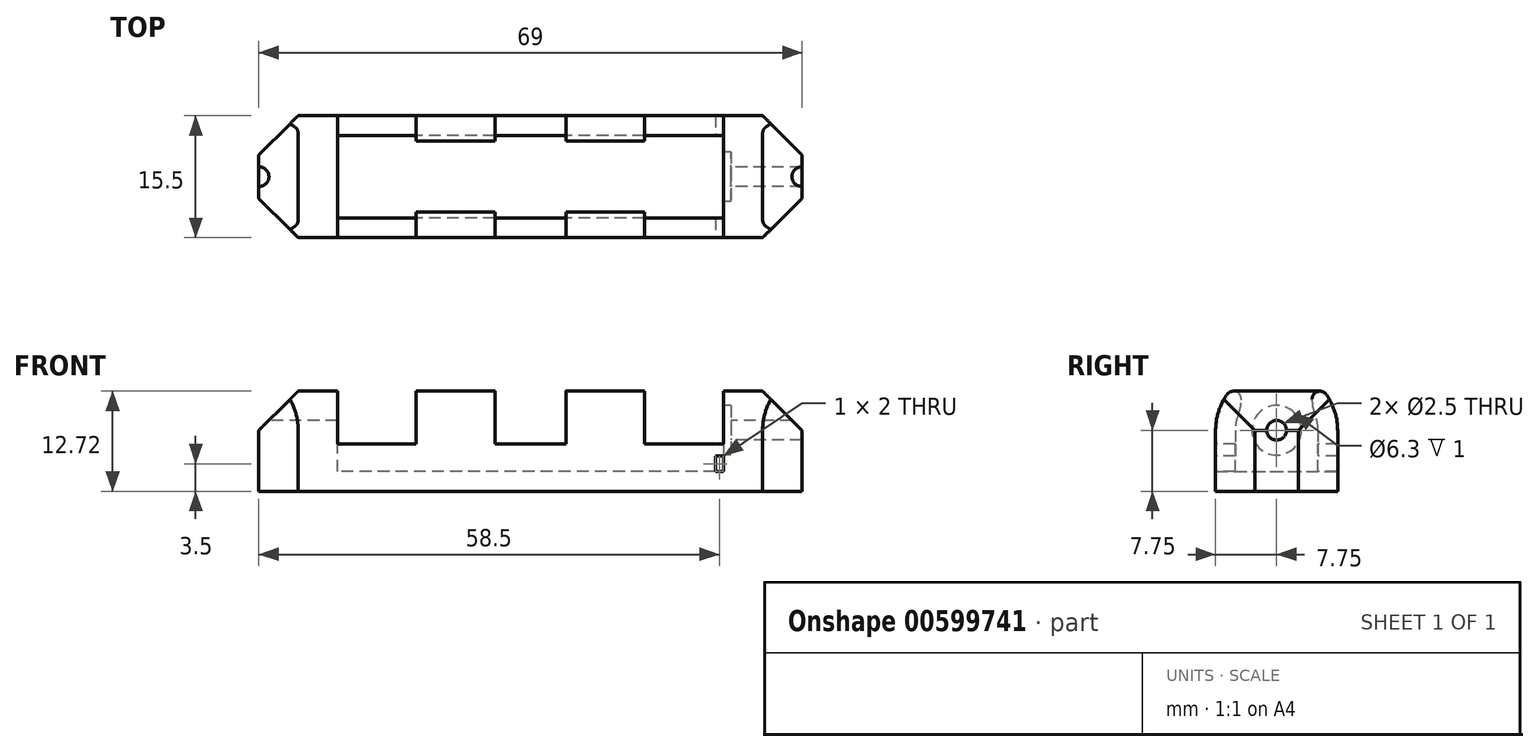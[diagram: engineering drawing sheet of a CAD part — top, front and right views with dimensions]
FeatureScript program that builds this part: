
annotation { "Feature Type Name" : "Feature", "Feature Type Description" : "" }
export const myFeature = defineFeature(function(context is Context, id is Id, definition is map)
    precondition{}
    {
        {
            var Q0;
            Q0=qCreatedBy(makeId("Top.planeOp"),FACE);
            var sketch = newSketch(context, id + "F0", { "sketchPlane" : qUnion([Q0])});
            skLineSegment(sketch, "E0.bottom", {"start": v(0, 0) * mm, "end": v(49, 0) * mm});
            skLineSegment(sketch, "E0.top", {"start": v(0, 15.5) * mm, "end": v(49, 15.5) * mm});
            skLineSegment(sketch, "E0.left", {"start": v(0, 0) * mm, "end": v(0, 15.5) * mm});
            skLineSegment(sketch, "E0.right", {"start": v(49, 0) * mm, "end": v(49, 15.5) * mm});
            skSolve(sketch);
        }
        {
            var Q0;
            Q0 = qSketchRegion(id + "F0", true);
            extrude(context, id + "F1", {"entities" : qUnion([Q0]), "depth" : 2.5 * mm, "offsetDistance" : 25 * mm});
        }
        {
            var Q0;
            Q0=qCreatedBy(makeId("Right.planeOp"),FACE);
            var sketch = newSketch(context, id + "F2", { "sketchPlane" : qUnion([Q0])});
            skLineSegment(sketch, "E1.0", {"start": v(0, 2.5) * mm, "end": v(15.5, 2.5) * mm});
            skLineSegment(sketch, "E2", {"start": v(15.5, 2.5) * mm, "end": v(15.5, 7.75) * mm});
            skArc(sketch, "E3", {"start": v(15.5, 7.75) * mm, "mid": v(14.64, 11.34) * mm, "end": v(12.25, 14.14) * mm});
            skLineSegment(sketch, "E4", {"start": v(7.75, 2.5) * mm, "end": v(7.75, 20.54) * mm, "construction": true});
            skArc(sketch, "E5.0", {"start": v(13, 7.75) * mm, "mid": v(12.8, 9.18) * mm, "end": v(12.25, 10.5) * mm});
            skLineSegment(sketch, "E5.1", {"start": v(13, 2.5) * mm, "end": v(13, 7.75) * mm});
            skLineSegment(sketch, "E6", {"start": v(12.25, 14.14) * mm, "end": v(12.25, 10.5) * mm});
            skArc(sketch, "E7.MirrorCS", {"start": v(2.5, 7.75) * mm, "mid": v(2.7, 9.18) * mm, "end": v(3.25, 10.5) * mm});
            skLineSegment(sketch, "E8.MirrorCS", {"start": v(3.25, 14.14) * mm, "end": v(3.25, 10.5) * mm});
            skArc(sketch, "E9.MirrorCS", {"start": v(0, 7.75) * mm, "mid": v(0.86, 11.34) * mm, "end": v(3.25, 14.14) * mm});
            skLineSegment(sketch, "E10.MirrorCS", {"start": v(0, 2.5) * mm, "end": v(0, 7.75) * mm});
            skLineSegment(sketch, "E11.MirrorCS", {"start": v(2.5, 2.5) * mm, "end": v(2.5, 7.75) * mm});
            skCircle(sketch, "E12", {"center": v(7.75, 7.75) * mm, "radius": 5.25 * mm, "construction": true});
            skSolve(sketch);
        }
        {
            var Q0;
            Q0 = qSketchRegion(id + "F2", true);
            var Q1;
            Q1=makeQuery(id+"F1.opExtrude","SWEPT_FACE",FACE,{"disambiguationData":[OSD([sQuery(id+"F0.wireOp",EDGE,"E0.right")])]});
            extrude(context, id + "F3", {"entities" : qUnion([Q0]), "operationType" : NewBodyOperationType.ADD, "endBound" : BoundingType.UP_TO_SURFACE, "depth" : 25 * mm, "endBoundEntityFace" : qUnion([Q1]), "offsetDistance" : 25 * mm});
        }
        {
            var Q0;
            Q0=makeQuery(id+"F3.opExtrude","SWEPT_EDGE",EDGE,{"disambiguationData":[OSD([sQuery(id+"F2.wireOp",EDGE,"E3"),sQuery(id+"F2.wireOp",EDGE,"E6")])]});
            var Q1;
            Q1=makeQuery(id+"F3.opExtrude","SWEPT_EDGE",EDGE,{"disambiguationData":[OSD([sQuery(id+"F2.wireOp",EDGE,"E8.MirrorCS"),sQuery(id+"F2.wireOp",EDGE,"E9.MirrorCS")])]});
            fillet(context, id + "F4", {"entities" : qUnion([Q0, Q1]), "radius" : 1 * mm, "tangentPropagation" : true, "allowEdgeOverflow" : false});
        }
        {
            var Q0;
            Q0=makeQuery(id+"F3.opExtrude","SWEPT_EDGE",EDGE,{"disambiguationData":[OSD([sQuery(id+"F2.wireOp",EDGE,"E5.0"),sQuery(id+"F2.wireOp",EDGE,"E6")])]});
            var Q1;
            Q1=makeQuery(id+"F3.opExtrude","SWEPT_EDGE",EDGE,{"disambiguationData":[OSD([sQuery(id+"F2.wireOp",EDGE,"E7.MirrorCS"),sQuery(id+"F2.wireOp",EDGE,"E8.MirrorCS")])]});
            fillet(context, id + "F5", {"entities" : qUnion([Q0, Q1]), "radius" : 5 * mm, "tangentPropagation" : true, "allowEdgeOverflow" : false});
        }
        {
            var Q0;
            {var subQ0=sQuery(id+"F2.wireOp",EDGE,"E1.0");Q0=makeQuery(id+"F3.boolean.opBoolean","MERGE",FACE,{"derivedFrom":[makeQuery(id+"F1.opExtrude","SWEPT_FACE",FACE,{"disambiguationData":[OSD([sQuery(id+"F0.wireOp",EDGE,"E0.left")])]}),makeQuery(id+"F3.opExtrude","CAP_FACE",FACE,{"disambiguationData":[OSD([subQ0,sQuery(id+"F2.wireOp",EDGE,"E7.MirrorCS"),sQuery(id+"F2.wireOp",EDGE,"E8.MirrorCS"),sQuery(id+"F2.wireOp",EDGE,"E9.MirrorCS"),sQuery(id+"F2.wireOp",EDGE,"E10.MirrorCS"),sQuery(id+"F2.wireOp",EDGE,"E11.MirrorCS")])],"isStart":true}),makeQuery(id+"F3.opExtrude","CAP_FACE",FACE,{"disambiguationData":[OSD([subQ0,sQuery(id+"F2.wireOp",EDGE,"E2"),sQuery(id+"F2.wireOp",EDGE,"E3"),sQuery(id+"F2.wireOp",EDGE,"E5.0"),sQuery(id+"F2.wireOp",EDGE,"E5.1"),sQuery(id+"F2.wireOp",EDGE,"E6")])],"isStart":true})]});}
            var sketch = newSketch(context, id + "F6", { "sketchPlane" : qUnion([Q0])});
            skArc(sketch, "E13.0", {"start": v(-15.5, 7.75) * mm, "mid": v(-15.13, 10.13) * mm, "end": v(-14.07, 12.29) * mm});
            skArc(sketch, "E14.0", {"start": v(-13.25, 12.72) * mm, "mid": v(-13.71, 12.6) * mm, "end": v(-14.07, 12.29) * mm});
            skLineSegment(sketch, "E15.0", {"start": v(-15.5, 7.75) * mm, "end": v(-15.5, 0) * mm});
            skLineSegment(sketch, "E16.0", {"start": v(0, 0) * mm, "end": v(-15.5, 0) * mm});
            skLineSegment(sketch, "E17.0", {"start": v(0, 7.75) * mm, "end": v(0, 0) * mm});
            skArc(sketch, "E18.0", {"start": v(0, 7.75) * mm, "mid": v(-0.37, 10.13) * mm, "end": v(-1.43, 12.29) * mm});
            skArc(sketch, "E19.0", {"start": v(-1.43, 12.29) * mm, "mid": v(-1.79, 12.6) * mm, "end": v(-2.25, 12.72) * mm});
            skLineSegment(sketch, "E20", {"start": v(-13.25, 11.72) * mm, "end": v(-13.25, 12.72) * mm, "construction": true});
            skLineSegment(sketch, "E21", {"start": v(-2.25, 11.72) * mm, "end": v(-2.25, 12.72) * mm, "construction": true});
            skLineSegment(sketch, "E22", {"start": v(-13.25, 12.72) * mm, "end": v(-2.25, 12.72) * mm});
            skSolve(sketch);
        }
        {
            var Q0;
            Q0 = qSketchRegion(id + "F6", true);
            extrude(context, id + "F7", {"entities" : qUnion([Q0]), "operationType" : NewBodyOperationType.ADD, "depth" : 10 * mm, "offsetDistance" : 25 * mm});
        }
        {
            var Q0;
            {var subQ0=sQuery(id+"F0.wireOp",EDGE,"E0.right");Q0=makeQuery(id+"F3.boolean.opBoolean","MERGE",FACE,{"derivedFrom":[makeQuery(id+"F1.opExtrude","SWEPT_FACE",FACE,{"disambiguationData":[OSD([subQ0])]}),makeQuery(id+"F3.opExtrude","CAP_FACE",FACE,{"disambiguationData":[OSD([subQ0]),OD(0.0)],"isStart":false}),makeQuery(id+"F3.opExtrude","CAP_FACE",FACE,{"disambiguationData":[OSD([subQ0]),OD(1.0)],"isStart":false})]});}
            var sketch = newSketch(context, id + "F8", { "sketchPlane" : qUnion([Q0])});
            skArc(sketch, "E23.0", {"start": v(15.5, 7.75) * mm, "mid": v(15.13, 10.13) * mm, "end": v(14.07, 12.29) * mm});
            skArc(sketch, "E23.1", {"start": v(13.25, 12.72) * mm, "mid": v(13.71, 12.6) * mm, "end": v(14.07, 12.29) * mm});
            skLineSegment(sketch, "E23.2", {"start": v(15.5, 7.75) * mm, "end": v(15.5, 0) * mm});
            skLineSegment(sketch, "E23.3", {"start": v(0, 0) * mm, "end": v(15.5, 0) * mm});
            skLineSegment(sketch, "E23.4", {"start": v(0, 7.75) * mm, "end": v(0, 0) * mm});
            skArc(sketch, "E23.5", {"start": v(0, 7.75) * mm, "mid": v(0.37, 10.13) * mm, "end": v(1.43, 12.29) * mm});
            skArc(sketch, "E23.6", {"start": v(1.43, 12.29) * mm, "mid": v(1.79, 12.6) * mm, "end": v(2.25, 12.72) * mm});
            skLineSegment(sketch, "E23.7", {"start": v(13.25, 11.72) * mm, "end": v(13.25, 12.72) * mm});
            skLineSegment(sketch, "E23.8", {"start": v(2.25, 11.72) * mm, "end": v(2.25, 12.72) * mm});
            skLineSegment(sketch, "E23.9", {"start": v(13.25, 12.72) * mm, "end": v(2.25, 12.72) * mm});
            skSolve(sketch);
        }
        {
            var Q0;
            Q0 = qSketchRegion(id + "F8", true);
            extrude(context, id + "F9", {"entities" : qUnion([Q0]), "operationType" : NewBodyOperationType.ADD, "depth" : 10 * mm, "offsetDistance" : 25 * mm});
        }
        {
            var Q0;
            Q0=makeQuery(id+"F3.boolean.opBoolean","MERGE",FACE,{"derivedFrom":[makeQuery(id+"F1.opExtrude","SWEPT_FACE",FACE,{"disambiguationData":[OSD([sQuery(id+"F0.wireOp",EDGE,"E0.bottom")])]}),makeQuery(id+"F3.opExtrude","SWEPT_FACE",FACE,{"disambiguationData":[OSD([sQuery(id+"F2.wireOp",EDGE,"E10.MirrorCS")])]})]});
            var sketch = newSketch(context, id + "F10", { "sketchPlane" : qUnion([Q0])});
            skPoint(sketch, "E24.0", {"position": v(0, 12.72) * mm});
            skPoint(sketch, "E25.0", {"position": v(49, 12.72) * mm});
            skLineSegment(sketch, "E26.bottom", {"start": v(0, 12.72) * mm, "end": v(10, 12.72) * mm});
            skLineSegment(sketch, "E26.left", {"start": v(0, 12.72) * mm, "end": v(0, 6) * mm});
            skLineSegment(sketch, "E26.right", {"start": v(10, 12.72) * mm, "end": v(10, 6) * mm});
            skLineSegment(sketch, "E27.top", {"start": v(20, 12.72) * mm, "end": v(29, 12.72) * mm});
            skLineSegment(sketch, "E27.left", {"start": v(20, 6) * mm, "end": v(20, 12.72) * mm});
            skLineSegment(sketch, "E27.right", {"start": v(29, 6) * mm, "end": v(29, 12.72) * mm});
            skLineSegment(sketch, "E28.bottom", {"start": v(49, 12.72) * mm, "end": v(39, 12.72) * mm});
            skLineSegment(sketch, "E28.left", {"start": v(49, 12.72) * mm, "end": v(49, 6) * mm});
            skLineSegment(sketch, "E28.right", {"start": v(39, 12.72) * mm, "end": v(39, 6) * mm});
            skPoint(sketch, "E29.orphan", {"position": v(0, 6) * mm});
            skLineSegment(sketch, "E30", {"start": v(0, 6) * mm, "end": v(49, 6) * mm});
            skSolve(sketch);
        }
        {
            var Q0;
            Q0 = qSketchRegion(id + "F10", true);
            extrude(context, id + "F11", {"entities" : qUnion([Q0]), "operationType" : NewBodyOperationType.REMOVE, "endBound" : BoundingType.THROUGH_ALL, "oppositeDirection" : true, "depth" : 25 * mm, "offsetDistance" : 25 * mm});
        }
        {
            var Q0;
            Q0=makeQuery(id+"F7.opExtrude","CAP_EDGE",EDGE,{"disambiguationData":[OSD([sQuery(id+"F6.wireOp",EDGE,"E22")])],"isStart":false});
            var Q1;
            Q1=makeQuery(id+"F9.opExtrude","CAP_EDGE",EDGE,{"disambiguationData":[OSD([sQuery(id+"F8.wireOp",EDGE,"E23.9")])],"isStart":false});
            var Q2;
            Q2=makeQuery(id+"F7.opExtrude","CAP_EDGE",EDGE,{"disambiguationData":[OSD([sQuery(id+"F6.wireOp",EDGE,"E17.0")])],"isStart":false});
            var Q3;
            Q3=makeQuery(id+"F7.opExtrude","CAP_EDGE",EDGE,{"disambiguationData":[OSD([sQuery(id+"F6.wireOp",EDGE,"E15.0")])],"isStart":false});
            var Q4;
            Q4=makeQuery(id+"F9.opExtrude","CAP_EDGE",EDGE,{"disambiguationData":[OSD([sQuery(id+"F8.wireOp",EDGE,"E23.4")])],"isStart":false});
            var Q5;
            Q5=makeQuery(id+"F9.opExtrude","CAP_EDGE",EDGE,{"disambiguationData":[OSD([sQuery(id+"F8.wireOp",EDGE,"E23.2")])],"isStart":false});
            chamfer(context, id + "F12", {"entities" : qUnion([Q0, Q1, Q2, Q3, Q4, Q5]), "width" : 5 * mm});
        }
        {
            var Q0;
            Q0=makeQuery(id+"F7.opExtrude","CAP_FACE",FACE,{"disambiguationData":[OSD([sQuery(id+"F6.wireOp",EDGE,"E13.0"),sQuery(id+"F6.wireOp",EDGE,"E14.0"),sQuery(id+"F6.wireOp",EDGE,"E15.0"),sQuery(id+"F6.wireOp",EDGE,"E16.0"),sQuery(id+"F6.wireOp",EDGE,"E17.0"),sQuery(id+"F6.wireOp",EDGE,"E18.0"),sQuery(id+"F6.wireOp",EDGE,"E19.0"),sQuery(id+"F6.wireOp",EDGE,"E22")])],"isStart":false});
            var sketch = newSketch(context, id + "F13", { "sketchPlane" : qUnion([Q0])});
            skLineSegment(sketch, "E31.0", {"start": v(-2.5, 2.5) * mm, "end": v(-13, 2.5) * mm, "construction": true});
            skCircle(sketch, "E32", {"center": v(-7.75, 7.75) * mm, "radius": 5.25 * mm, "construction": true});
            skLineSegment(sketch, "E33", {"start": v(-7.75, 2.5) * mm, "end": v(-7.75, 12.86) * mm, "construction": true});
            skCircle(sketch, "E34", {"center": v(-7.75, 7.75) * mm, "radius": 1.25 * mm});
            skSolve(sketch);
        }
        {
            var Q0;
            Q0 = qSketchRegion(id + "F13", true);
            extrude(context, id + "F14", {"entities" : qUnion([Q0]), "operationType" : NewBodyOperationType.REMOVE, "endBound" : BoundingType.THROUGH_ALL, "oppositeDirection" : true, "depth" : 25 * mm, "offsetDistance" : 25 * mm});
        }
        {
            var Q0;
            Q0=makeQuery(id+"F9.boolean.opBoolean","MERGE",FACE,{"derivedFrom":[makeQuery(id+"F7.boolean.opBoolean","MERGE",FACE,{"derivedFrom":[makeQuery(id+"F3.boolean.opBoolean","MERGE",FACE,{"derivedFrom":[makeQuery(id+"F1.opExtrude","SWEPT_FACE",FACE,{"disambiguationData":[OSD([sQuery(id+"F0.wireOp",EDGE,"E0.bottom")])]}),makeQuery(id+"F3.opExtrude","SWEPT_FACE",FACE,{"disambiguationData":[OSD([sQuery(id+"F2.wireOp",EDGE,"E10.MirrorCS")])]})]}),makeQuery(id+"F7.opExtrude","SWEPT_FACE",FACE,{"disambiguationData":[OSD([sQuery(id+"F6.wireOp",EDGE,"E17.0")])]})]}),makeQuery(id+"F9.opExtrude","SWEPT_FACE",FACE,{"disambiguationData":[OSD([sQuery(id+"F8.wireOp",EDGE,"E23.4")])]})]});
            var sketch = newSketch(context, id + "F15", { "sketchPlane" : qUnion([Q0])});
            skLineSegment(sketch, "E35.0", {"start": v(49, 2.5) * mm, "end": v(0, 2.5) * mm, "construction": true});
            skLineSegment(sketch, "E36.bottom", {"start": v(49, 2.5) * mm, "end": v(48, 2.5) * mm});
            skLineSegment(sketch, "E36.top", {"start": v(49, 4.5) * mm, "end": v(48, 4.5) * mm});
            skLineSegment(sketch, "E36.left", {"start": v(49, 2.5) * mm, "end": v(49, 4.5) * mm});
            skLineSegment(sketch, "E36.right", {"start": v(48, 2.5) * mm, "end": v(48, 4.5) * mm});
            skSolve(sketch);
        }
        {
            var Q0;
            Q0=makeQuery(id+"F15.imprint","IMPRINT",FACE,{"disambiguationData":[TD([[makeQuery(id+"F15.imprint","IMPRINT",EDGE,{"derivedFrom":sQuery(id+"F15.wireOp",EDGE,"E36.bottom")}),-1.0]])]});
            extrude(context, id + "F16", {"entities" : qUnion([Q0]), "operationType" : NewBodyOperationType.REMOVE, "endBound" : BoundingType.THROUGH_ALL, "oppositeDirection" : true, "depth" : 25 * mm, "offsetDistance" : 25 * mm});
        }
        {
            var Q0;
            Q0=makeQuery(id+"F16.boolean.opBoolean","MERGE",FACE,{"derivedFrom":[makeQuery(id+"F11.boolean.opBoolean","MERGE",FACE,{"derivedFrom":[makeQuery(id+"F9.opExtrude","CAP_FACE",FACE,{"disambiguationData":[OSD([sQuery(id+"F8.wireOp",EDGE,"E23.0"),sQuery(id+"F8.wireOp",EDGE,"E23.1"),sQuery(id+"F8.wireOp",EDGE,"E23.2"),sQuery(id+"F8.wireOp",EDGE,"E23.3"),sQuery(id+"F8.wireOp",EDGE,"E23.4"),sQuery(id+"F8.wireOp",EDGE,"E23.5"),sQuery(id+"F8.wireOp",EDGE,"E23.6"),sQuery(id+"F8.wireOp",EDGE,"E23.9")])],"isStart":true}),makeQuery(id+"F11.opExtrude","SWEPT_FACE",FACE,{"disambiguationData":[OSD([sQuery(id+"F10.wireOp",EDGE,"E28.left")])]})]}),makeQuery(id+"F16.opExtrude","SWEPT_FACE",FACE,{"disambiguationData":[OSD([sQuery(id+"F15.wireOp",EDGE,"E36.left")])]})]});
            var sketch = newSketch(context, id + "F17", { "sketchPlane" : qUnion([Q0])});
            skCircle(sketch, "E37.0", {"center": v(-7.75, 7.75) * mm, "radius": 1.25 * mm, "construction": true});
            skCircle(sketch, "E38", {"center": v(-7.75, 7.75) * mm, "radius": 3.15 * mm});
            skSolve(sketch);
        }
        {
            var Q0;
            Q0 = qSketchRegion(id + "F17", true);
            extrude(context, id + "F18", {"entities" : qUnion([Q0]), "operationType" : NewBodyOperationType.REMOVE, "oppositeDirection" : true, "depth" : 1 * mm, "offsetDistance" : 25 * mm});
        }
    });
